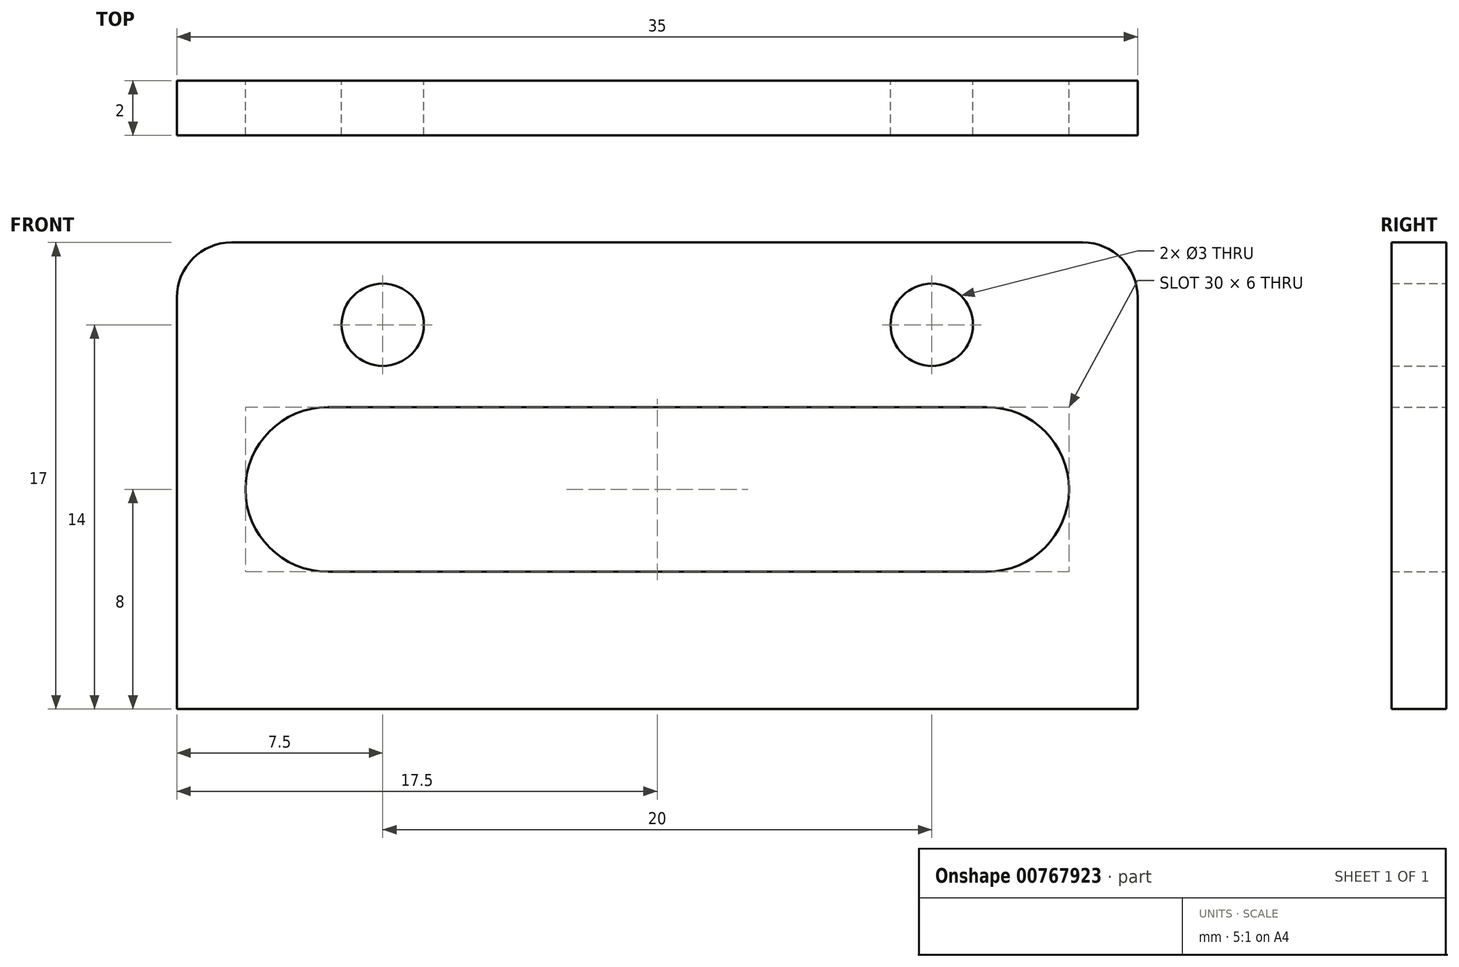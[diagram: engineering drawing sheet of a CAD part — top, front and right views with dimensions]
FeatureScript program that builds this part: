
annotation { "Feature Type Name" : "Feature", "Feature Type Description" : "" }
export const myFeature = defineFeature(function(context is Context, id is Id, definition is map)
    precondition{}
    {
        {
            var Q0;
            Q0=qCreatedBy(makeId("Front.planeOp"),FACE);
            var sketch = newSketch(context, id + "F0", { "sketchPlane" : qUnion([Q0])});
            skCircle(sketch, "E0", {"center": v(9, 14) * mm, "radius": 1.5 * mm});
            skCircle(sketch, "E1.MirrorC", {"center": v(29, 14) * mm, "radius": 1.5 * mm});
            skLineSegment(sketch, "E2.bottom", {"start": v(3.5, 17) * mm, "end": v(34.5, 17) * mm});
            skLineSegment(sketch, "E2.top", {"start": v(1.5, 0) * mm, "end": v(36.5, 0) * mm});
            skLineSegment(sketch, "E2.left", {"start": v(1.5, 15) * mm, "end": v(1.5, 0) * mm});
            skLineSegment(sketch, "E2.right", {"start": v(36.5, 15) * mm, "end": v(36.5, 0) * mm});
            skLineSegment(sketch, "E3.bottom", {"start": v(7, 11) * mm, "end": v(31, 11) * mm});
            skLineSegment(sketch, "E3.top", {"start": v(7, 5) * mm, "end": v(31, 5) * mm});
            skLineSegment(sketch, "E4", {"start": v(19, 17) * mm, "end": v(19, 0) * mm, "construction": true});
            skArc(sketch, "E5", {"start": v(7, 11) * mm, "mid": v(4, 8) * mm, "end": v(7, 5) * mm});
            skArc(sketch, "E6.MirrorCS", {"start": v(31, 11) * mm, "mid": v(34, 8) * mm, "end": v(31, 5) * mm});
            skPoint(sketch, "E7.visualSharp", {"position": v(1.5, 17) * mm});
            skArc(sketch, "E7.filletArc", {"start": v(3.5, 17) * mm, "mid": v(2.09, 16.41) * mm, "end": v(1.5, 15) * mm});
            skPoint(sketch, "E8.visualSharp", {"position": v(36.5, 17) * mm});
            skArc(sketch, "E8.filletArc", {"start": v(36.5, 15) * mm, "mid": v(35.91, 16.41) * mm, "end": v(34.5, 17) * mm});
            skSolve(sketch);
        }
        {
            var Q0;
            Q0=makeQuery(id+"F0.imprint","IMPRINT",FACE,{"disambiguationData":[TD([[makeQuery(id+"F0.imprint","IMPRINT",EDGE,{"derivedFrom":sQuery(id+"F0.wireOp",EDGE,"E0")}),-1.0]])]});
            extrude(context, id + "F1", {"entities" : qUnion([Q0]), "depth" : 2 * mm, "offsetDistance" : 25 * mm});
        }
    });
